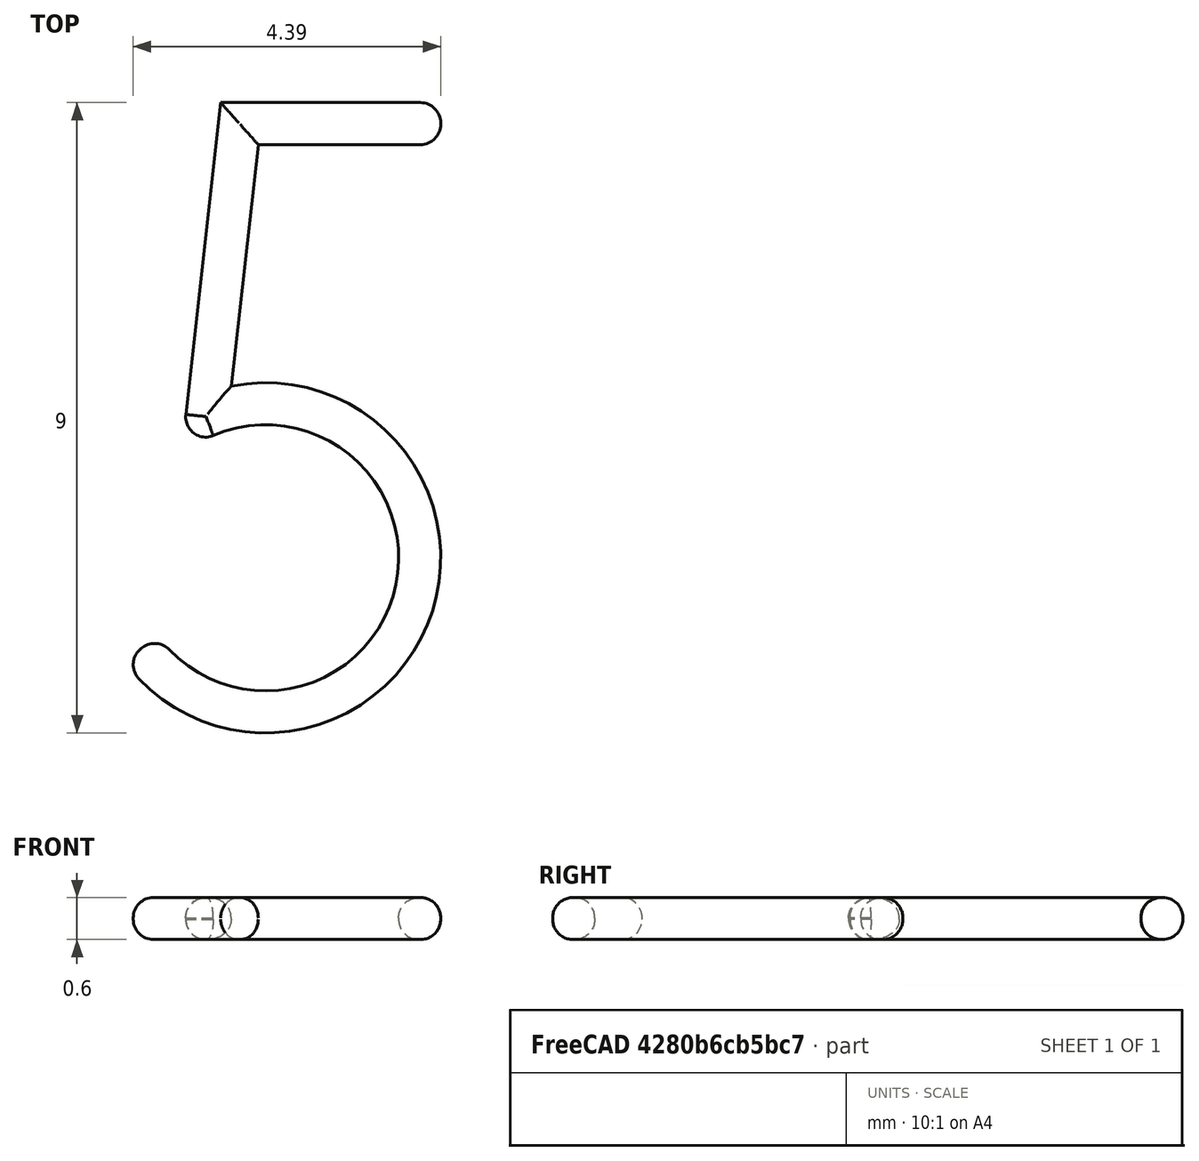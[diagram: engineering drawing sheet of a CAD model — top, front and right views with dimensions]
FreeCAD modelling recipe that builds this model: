
FCSTD DOCUMENT  (FreeCAD 0.16R6712 (Git))
Label: 5s
License: All rights reserved
LicenseURL: http://en.wikipedia.org/wiki/All_rights_reserved
objects: Sketcher::SketchObject×1, PartDesign::Pad×1, PartDesign::Fillet×1, Mesh::Feature×1
note: 4 computed .brp shape members not serialized (recipe doc carries the construction recipe); baked Part::Feature solids carry a one-line shape summary decoded from their .brp

FEATURE [Sketcher::SketchObject] Sketch
  sketch-geometry (9):
    g0: ArcOfCircle CenterX=0 CenterY=2.5 CenterZ=0 NormalX=0 NormalY=0 NormalZ=1 Radius=2.5 StartAngle=3.77091 EndAngle=8.05168
    g1: LineSegment StartX=-0.491033 StartY=4.9513 StartZ=0 EndX=-0.104775 EndY=8.4 EndZ=0
    g2: LineSegment StartX=-0.104775 StartY=8.4 StartZ=0 EndX=2.5 EndY=8.4 EndZ=0
    g3: LineSegment StartX=-0.641326 StartY=9 StartZ=0 EndX=2.5 EndY=9 EndZ=0
    g4: LineSegment StartX=-0.641326 StartY=9 StartZ=0 EndX=-1.14021 EndY=4.54571 EndZ=0
    g5: ArcOfCircle CenterX=0 CenterY=2.5 CenterZ=0 NormalX=0 NormalY=0 NormalZ=1 Radius=1.9 StartAngle=3.77091 EndAngle=8.25944
    g6: LineSegment StartX=-1.53602 StartY=1.38168 StartZ=0 EndX=-2.02108 EndY=1.02853 EndZ=0
    g7: LineSegment StartX=2.5 StartY=8.4 StartZ=0 EndX=2.5 EndY=9 EndZ=0
    g8: ArcOfCircle CenterX=-0.854407 CenterY=4.5137 CenterZ=0 NormalX=0 NormalY=0 NormalZ=1 Radius=0.287591 StartAngle=3.03007 EndAngle=5.08605
  constraints (24):
    c: PointOnObject(g0,g-2)
    c: Coincident(g1,g0)
    c: Coincident(g2,g1)
    c: Horizontal(g2)
    c: Tangent(g0,g-1)
    c: Radius(g0) = 2.5
    c: Horizontal(g3)
    c: Coincident(g4,g3)
    c: Coincident(g5,g0)
    c: Coincident(g6,g5)
    c: Coincident(g6,g0)
    c: Perpendicular(g0,g6)
    c: Distance(g5,g0) = 0.6
    c: DistanceX(g-1,g2) = 2.5
    c: Coincident(g7,g3)
    c: Perpendicular(g7,g2)
    c: Coincident(g7,g2)
    c: Coincident(g8,g4)
    c: Coincident(g8,g5)
    c: Tangent(g8,g4)
    c: DistanceY(g2,g3) = 0.6
    c: Distance(g-1,g3) = 9
    c: Parallel(g1,g4)
    c: Distance(g1,g4) = 0.6
FEATURE [PartDesign::Pad] Pad
  Length = 0.6
  Length2 = 100
  Midplane = true
  Sketch = -> Sketch
  Type = 0
FEATURE [PartDesign::Fillet] Fillet
  Base = -> Pad [Edge4,Edge7,Edge10,Edge13,Edge16,Edge19,Edge22,Edge25,Edge27,Edge11,Edge14,Edge15,Edge3,Edge6,Edge9,Edge12,Edge18,Edge21,Edge24,Edge26,Edge1,Edge2]
  Radius = 0.29
FEATURE [Mesh::Feature] Mesh  label="Fillet (Meshed)"
